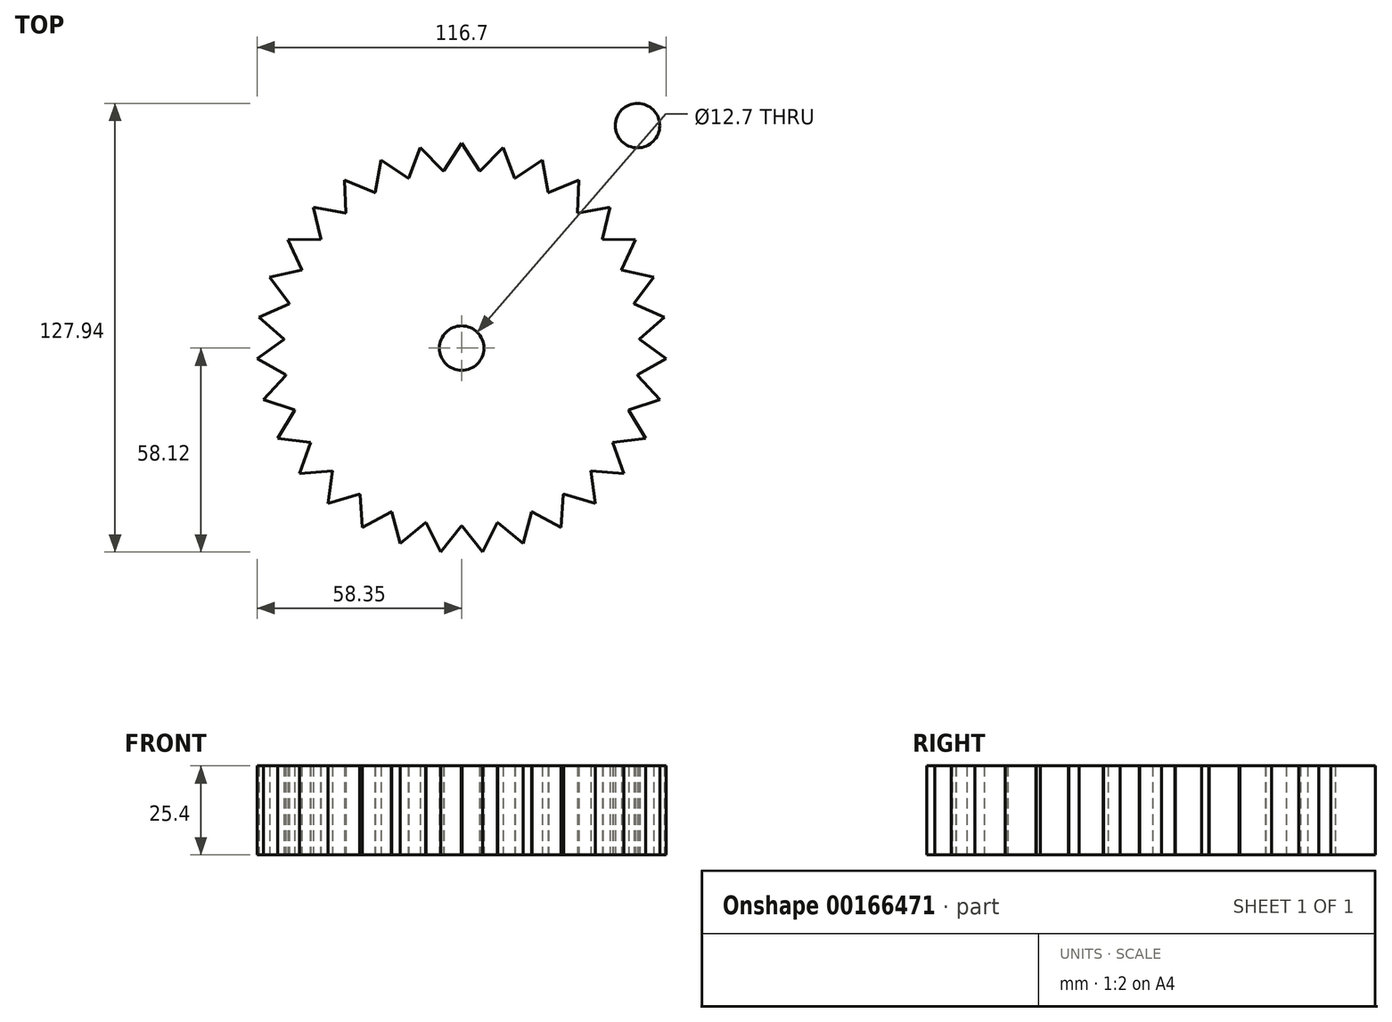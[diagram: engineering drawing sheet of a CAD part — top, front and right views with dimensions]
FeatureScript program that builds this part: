
annotation { "Feature Type Name" : "Feature", "Feature Type Description" : "" }
export const myFeature = defineFeature(function(context is Context, id is Id, definition is map)
    precondition{}
    {
        {
            var Q0;
            Q0=qCreatedBy(makeId("Top.planeOp"),FACE);
            var sketch = newSketch(context, id + "F0", { "sketchPlane" : qUnion([Q0])});
            skCircle(sketch, "E0", {"center": v(0, 0) * mm, "radius": 50.8 * mm});
            skLineSegment(sketch, "E1", {"start": v(0, 50.8) * mm, "end": v(0, 58.42) * mm});
            skLineSegment(sketch, "E2", {"start": v(0, 58.42) * mm, "end": v(5.07, 50.55) * mm});
            skLineSegment(sketch, "E3", {"start": v(5.07, 50.55) * mm, "end": v(0, 58.42) * mm});
            skLineSegment(sketch, "E4", {"start": v(0, 58.42) * mm, "end": v(-5.07, 50.55) * mm});
            skLineSegment(sketch, "E5.1.0", {"start": v(-5.2, 50.53) * mm, "end": v(-11.76, 57.22) * mm});
            skLineSegment(sketch, "E5.1.1", {"start": v(-11.76, 57.22) * mm, "end": v(-15.14, 48.5) * mm});
            skLineSegment(sketch, "E5.2.0", {"start": v(-15.27, 48.45) * mm, "end": v(-23.04, 53.69) * mm});
            skLineSegment(sketch, "E5.2.1", {"start": v(-23.04, 53.69) * mm, "end": v(-24.6, 44.45) * mm});
            skLineSegment(sketch, "E5.3.0", {"start": v(-24.71, 44.38) * mm, "end": v(-33.37, 47.95) * mm});
            skLineSegment(sketch, "E5.3.1", {"start": v(-33.37, 47.95) * mm, "end": v(-33.04, 38.59) * mm});
            skLineSegment(sketch, "E5.4.0", {"start": v(-33.14, 38.5) * mm, "end": v(-42.34, 40.25) * mm});
            skLineSegment(sketch, "E5.4.1", {"start": v(-42.34, 40.25) * mm, "end": v(-40.13, 31.15) * mm});
            skLineSegment(sketch, "E5.5.0", {"start": v(-40.21, 31.04) * mm, "end": v(-49.58, 30.9) * mm});
            skLineSegment(sketch, "E5.5.1", {"start": v(-49.58, 30.9) * mm, "end": v(-45.58, 22.43) * mm});
            skLineSegment(sketch, "E5.6.0", {"start": v(-45.64, 22.31) * mm, "end": v(-54.78, 20.29) * mm});
            skLineSegment(sketch, "E5.6.1", {"start": v(-54.78, 20.29) * mm, "end": v(-49.16, 12.8) * mm});
            skLineSegment(sketch, "E5.7.0", {"start": v(-49.2, 12.67) * mm, "end": v(-57.75, 8.85) * mm});
            skLineSegment(sketch, "E5.7.1", {"start": v(-57.75, 8.85) * mm, "end": v(-50.73, 2.64) * mm});
            skLineSegment(sketch, "E5.8.0", {"start": v(-50.74, 2.5) * mm, "end": v(-58.35, -2.96) * mm});
            skLineSegment(sketch, "E5.8.1", {"start": v(-58.35, -2.96) * mm, "end": v(-50.22, -7.63) * mm});
            skLineSegment(sketch, "E5.9.0", {"start": v(-50.2, -7.76) * mm, "end": v(-56.56, -14.64) * mm});
            skLineSegment(sketch, "E5.9.1", {"start": v(-56.56, -14.64) * mm, "end": v(-47.66, -17.58) * mm});
            skLineSegment(sketch, "E5.10.0", {"start": v(-47.61, -17.7) * mm, "end": v(-52.45, -25.73) * mm});
            skLineSegment(sketch, "E5.10.1", {"start": v(-52.45, -25.73) * mm, "end": v(-43.15, -26.82) * mm});
            skLineSegment(sketch, "E5.11.0", {"start": v(-43.08, -26.93) * mm, "end": v(-46.2, -35.76) * mm});
            skLineSegment(sketch, "E5.11.1", {"start": v(-46.2, -35.76) * mm, "end": v(-36.86, -34.95) * mm});
            skLineSegment(sketch, "E5.12.0", {"start": v(-36.77, -35.05) * mm, "end": v(-38.05, -44.33) * mm});
            skLineSegment(sketch, "E5.12.1", {"start": v(-38.05, -44.33) * mm, "end": v(-29.07, -41.66) * mm});
            skLineSegment(sketch, "E5.13.0", {"start": v(-28.97, -41.73) * mm, "end": v(-28.35, -51.08) * mm});
            skLineSegment(sketch, "E5.13.1", {"start": v(-28.35, -51.08) * mm, "end": v(-20.1, -46.66) * mm});
            skLineSegment(sketch, "E5.14.0", {"start": v(-19.97, -46.7) * mm, "end": v(-17.49, -55.74) * mm});
            skLineSegment(sketch, "E5.14.1", {"start": v(-17.49, -55.74) * mm, "end": v(-10.3, -49.75) * mm});
            skLineSegment(sketch, "E5.15.0", {"start": v(-10.16, -49.77) * mm, "end": v(-5.91, -58.12) * mm});
            skLineSegment(sketch, "E5.15.1", {"start": v(-5.91, -58.12) * mm, "end": v(-0.07, -50.8) * mm});
            skLineSegment(sketch, "E5.16.0", {"start": v(0.07, -50.8) * mm, "end": v(5.91, -58.12) * mm});
            skLineSegment(sketch, "E5.16.1", {"start": v(5.91, -58.12) * mm, "end": v(10.16, -49.77) * mm});
            skLineSegment(sketch, "E5.17.0", {"start": v(10.3, -49.75) * mm, "end": v(17.49, -55.74) * mm});
            skLineSegment(sketch, "E5.17.1", {"start": v(17.49, -55.74) * mm, "end": v(19.97, -46.7) * mm});
            skLineSegment(sketch, "E5.18.0", {"start": v(20.1, -46.66) * mm, "end": v(28.35, -51.08) * mm});
            skLineSegment(sketch, "E5.18.1", {"start": v(28.35, -51.08) * mm, "end": v(28.97, -41.73) * mm});
            skLineSegment(sketch, "E5.19.0", {"start": v(29.07, -41.66) * mm, "end": v(38.05, -44.33) * mm});
            skLineSegment(sketch, "E5.19.1", {"start": v(38.05, -44.33) * mm, "end": v(36.77, -35.05) * mm});
            skLineSegment(sketch, "E5.20.0", {"start": v(36.86, -34.95) * mm, "end": v(46.2, -35.76) * mm});
            skLineSegment(sketch, "E5.20.1", {"start": v(46.2, -35.76) * mm, "end": v(43.08, -26.93) * mm});
            skLineSegment(sketch, "E5.21.0", {"start": v(43.15, -26.82) * mm, "end": v(52.45, -25.73) * mm});
            skLineSegment(sketch, "E5.21.1", {"start": v(52.45, -25.73) * mm, "end": v(47.61, -17.7) * mm});
            skLineSegment(sketch, "E5.22.0", {"start": v(47.66, -17.58) * mm, "end": v(56.56, -14.64) * mm});
            skLineSegment(sketch, "E5.22.1", {"start": v(56.56, -14.64) * mm, "end": v(50.2, -7.76) * mm});
            skLineSegment(sketch, "E5.23.0", {"start": v(50.22, -7.63) * mm, "end": v(58.35, -2.96) * mm});
            skLineSegment(sketch, "E5.23.1", {"start": v(58.35, -2.96) * mm, "end": v(50.74, 2.5) * mm});
            skLineSegment(sketch, "E5.24.0", {"start": v(50.73, 2.64) * mm, "end": v(57.75, 8.85) * mm});
            skLineSegment(sketch, "E5.24.1", {"start": v(57.75, 8.85) * mm, "end": v(49.2, 12.67) * mm});
            skLineSegment(sketch, "E5.25.0", {"start": v(49.16, 12.8) * mm, "end": v(54.78, 20.29) * mm});
            skLineSegment(sketch, "E5.25.1", {"start": v(54.78, 20.29) * mm, "end": v(45.64, 22.31) * mm});
            skLineSegment(sketch, "E5.26.0", {"start": v(45.58, 22.43) * mm, "end": v(49.58, 30.9) * mm});
            skLineSegment(sketch, "E5.26.1", {"start": v(49.58, 30.9) * mm, "end": v(40.21, 31.04) * mm});
            skLineSegment(sketch, "E5.27.0", {"start": v(40.13, 31.15) * mm, "end": v(42.34, 40.25) * mm});
            skLineSegment(sketch, "E5.27.1", {"start": v(42.34, 40.25) * mm, "end": v(33.14, 38.5) * mm});
            skLineSegment(sketch, "E6.1.28.0", {"start": v(33.04, 38.59) * mm, "end": v(33.37, 47.95) * mm});
            skLineSegment(sketch, "E6.3.28.0", {"start": v(33.37, 47.95) * mm, "end": v(24.71, 44.38) * mm});
            skLineSegment(sketch, "E7.1.29.0", {"start": v(24.6, 44.45) * mm, "end": v(23.04, 53.69) * mm});
            skLineSegment(sketch, "E7.3.29.0", {"start": v(23.04, 53.69) * mm, "end": v(15.27, 48.45) * mm});
            skLineSegment(sketch, "E8.1.30.0", {"start": v(15.14, 48.5) * mm, "end": v(11.76, 57.22) * mm});
            skLineSegment(sketch, "E8.3.30.0", {"start": v(11.76, 57.22) * mm, "end": v(5.2, 50.53) * mm});
            skCircle(sketch, "E9", {"center": v(0, 0) * mm, "radius": 6.35 * mm});
            skSolve(sketch);
        }
        {
            var Q0;
            Q0 = qSketchRegion(id + "F0", true);
            extrude(context, id + "F1", {"entities" : qUnion([Q0]), "depth" : 25.4 * mm});
        }
        {
            var Q0;
            Q0=qCreatedBy(makeId("Top.planeOp"),FACE);
            var sketch = newSketch(context, id + "F2", { "sketchPlane" : qUnion([Q0])});
            skCircle(sketch, "E10", {"center": v(50.12, 63.47) * mm, "radius": 6.35 * mm});
            skSolve(sketch);
        }
        {
            var Q0;
            Q0=makeQuery(id+"F2.imprint","IMPRINT",FACE,{"disambiguationData":[TD([[makeQuery(id+"F2.imprint","IMPRINT",EDGE,{"derivedFrom":sQuery(id+"F2.wireOp",EDGE,"E10")}),1.0]])]});
            extrude(context, id + "F3", {"entities" : qUnion([Q0]), "depth" : 25.4 * mm});
        }
    });
